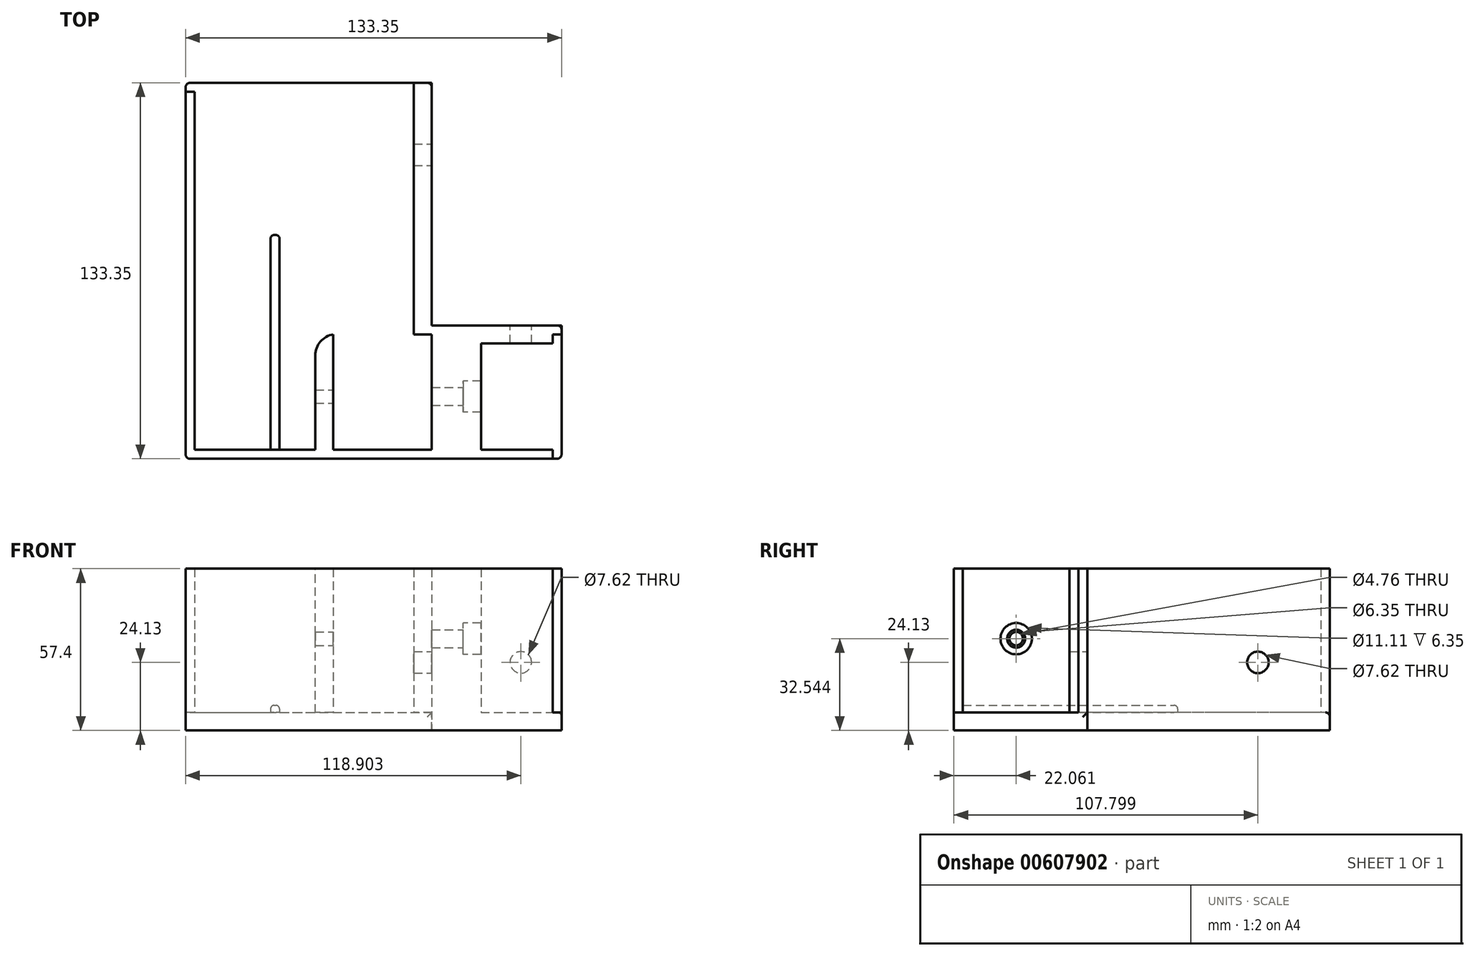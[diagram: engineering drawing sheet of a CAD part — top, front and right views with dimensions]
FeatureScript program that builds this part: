
annotation { "Feature Type Name" : "Feature", "Feature Type Description" : "" }
export const myFeature = defineFeature(function(context is Context, id is Id, definition is map)
    precondition{}
    {
        {
            var Q0;
            Q0=qCreatedBy(makeId("Top.planeOp"),FACE);
            var sketch = newSketch(context, id + "F0", { "sketchPlane" : qUnion([Q0])});
            skLineSegment(sketch, "E0.bottom", {"start": v(-63.28, 106.68) * mm, "end": v(70.07, 106.68) * mm});
            skLineSegment(sketch, "E0.top", {"start": v(-63.28, -26.67) * mm, "end": v(70.07, -26.67) * mm});
            skLineSegment(sketch, "E0.left", {"start": v(-63.28, 106.68) * mm, "end": v(-63.28, -26.67) * mm});
            skLineSegment(sketch, "E0.right", {"start": v(70.07, 106.68) * mm, "end": v(70.07, -26.67) * mm});
            skSolve(sketch);
        }
        {
            var Q0;
            Q0=makeQuery(id+"F0.imprint","IMPRINT",FACE,{"disambiguationData":[TD([[makeQuery(id+"F0.imprint","IMPRINT",EDGE,{"derivedFrom":sQuery(id+"F0.wireOp",EDGE,"E0.bottom")}),-1.0]])]});
            extrude(context, id + "F1", {"entities" : qUnion([Q0]), "depth" : 6.35 * mm, "offsetDistance" : 25.4 * mm});
        }
        {
            var Q0;
            Q0=makeQuery(id+"F1.opExtrude","CAP_FACE",FACE,{"disambiguationData":[OSD([sQuery(id+"F0.wireOp",EDGE,"E0.bottom"),sQuery(id+"F0.wireOp",EDGE,"E0.top"),sQuery(id+"F0.wireOp",EDGE,"E0.left"),sQuery(id+"F0.wireOp",EDGE,"E0.right")])],"isStart":false});
            var sketch = newSketch(context, id + "F2", { "sketchPlane" : qUnion([Q0])});
            skLineSegment(sketch, "E1.0", {"start": v(-60.1, 103.5) * mm, "end": v(66.9, 103.5) * mm});
            skLineSegment(sketch, "E1.1", {"start": v(-60.1, 103.5) * mm, "end": v(-60.1, -23.5) * mm});
            skLineSegment(sketch, "E1.2", {"start": v(-60.1, -23.5) * mm, "end": v(66.9, -23.5) * mm});
            skLineSegment(sketch, "E1.3", {"start": v(66.9, 103.5) * mm, "end": v(66.9, -23.5) * mm});
            skLineSegment(sketch, "E2.bottom", {"start": v(3.4, 103.5) * mm, "end": v(-10.9, 103.5) * mm});
            skLineSegment(sketch, "E2.top", {"start": v(3.4, -23.5) * mm, "end": v(-10.9, -23.5) * mm});
            skLineSegment(sketch, "E2.right", {"start": v(-10.9, 103.5) * mm, "end": v(-10.9, -23.5) * mm});
            skLineSegment(sketch, "E3.bottom", {"start": v(3.4, 103.5) * mm, "end": v(17.69, 103.5) * mm});
            skLineSegment(sketch, "E3.top", {"start": v(3.4, -23.5) * mm, "end": v(17.69, -23.5) * mm});
            skLineSegment(sketch, "E3.right", {"start": v(17.69, 103.5) * mm, "end": v(17.69, -23.5) * mm});
            skLineSegment(sketch, "E4.0", {"start": v(-17.25, 68.58) * mm, "end": v(-17.25, -23.5) * mm});
            skLineSegment(sketch, "E5.0", {"start": v(24.04, 68.58) * mm, "end": v(24.04, -23.5) * mm});
            skLineSegment(sketch, "E6", {"start": v(3.4, -23.5) * mm, "end": v(3.4, 103.5) * mm});
            skLineSegment(sketch, "E7", {"start": v(3.4, -23.5) * mm, "end": v(3.4, -3.18) * mm});
            skCircle(sketch, "E8", {"center": v(3.4, -3.18) * mm, "radius": 14.29 * mm});
            skLineSegment(sketch, "E9", {"start": v(3.4, 11.1) * mm, "end": v(3.4, 17.46) * mm});
            skLineSegment(sketch, "E10", {"start": v(17.69, 17.46) * mm, "end": v(-10.9, 17.46) * mm});
            skLineSegment(sketch, "E11", {"start": v(-10.9, 17.46) * mm, "end": v(-17.25, 17.46) * mm});
            skLineSegment(sketch, "E12", {"start": v(-60.1, 103.5) * mm, "end": v(-63.28, 103.5) * mm});
            skLineSegment(sketch, "E13", {"start": v(66.9, 103.5) * mm, "end": v(70.07, 103.5) * mm});
            skLineSegment(sketch, "E14", {"start": v(24.04, 68.58) * mm, "end": v(24.04, 103.5) * mm});
            skLineSegment(sketch, "E15", {"start": v(-17.25, 68.58) * mm, "end": v(-17.25, 103.5) * mm});
            skLineSegment(sketch, "E16", {"start": v(24.04, 103.5) * mm, "end": v(24.04, 106.68) * mm});
            skLineSegment(sketch, "E17", {"start": v(17.69, 103.5) * mm, "end": v(17.69, 106.68) * mm});
            skLineSegment(sketch, "E18", {"start": v(66.9, -23.5) * mm, "end": v(66.9, -26.67) * mm});
            skLineSegment(sketch, "E19", {"start": v(66.9, 17.46) * mm, "end": v(70.07, 17.46) * mm});
            skLineSegment(sketch, "E20.bottom", {"start": v(35.15, 17.46) * mm, "end": v(17.69, 17.46) * mm});
            skLineSegment(sketch, "E20.top", {"start": v(35.15, -23.5) * mm, "end": v(17.69, -23.5) * mm});
            skLineSegment(sketch, "E20.left", {"start": v(35.15, 17.46) * mm, "end": v(35.15, -23.5) * mm});
            skLineSegment(sketch, "E20.right", {"start": v(17.69, 17.46) * mm, "end": v(17.69, -23.5) * mm});
            skLineSegment(sketch, "E21", {"start": v(35.15, 17.46) * mm, "end": v(66.9, 17.46) * mm});
            skLineSegment(sketch, "E22", {"start": v(66.9, 17.46) * mm, "end": v(66.9, 20.63) * mm});
            skLineSegment(sketch, "E23", {"start": v(66.9, 20.63) * mm, "end": v(24.04, 20.63) * mm});
            skLineSegment(sketch, "E24", {"start": v(35.15, 17.46) * mm, "end": v(35.15, 14.28) * mm});
            skLineSegment(sketch, "E25", {"start": v(35.15, 14.28) * mm, "end": v(66.9, 14.28) * mm});
            skLineSegment(sketch, "E26.bottom", {"start": v(17.69, 103.5) * mm, "end": v(11.34, 103.5) * mm});
            skLineSegment(sketch, "E26.top", {"start": v(17.69, 97.15) * mm, "end": v(11.34, 97.15) * mm});
            skLineSegment(sketch, "E26.left", {"start": v(17.69, 103.5) * mm, "end": v(17.69, 97.15) * mm});
            skLineSegment(sketch, "E26.right", {"start": v(11.34, 103.5) * mm, "end": v(11.34, 97.15) * mm});
            skLineSegment(sketch, "E27.bottom", {"start": v(-60.1, 103.5) * mm, "end": v(-56.93, 103.5) * mm});
            skLineSegment(sketch, "E27.top", {"start": v(-60.1, 97.15) * mm, "end": v(-56.93, 97.15) * mm});
            skLineSegment(sketch, "E27.left", {"start": v(-60.1, 103.5) * mm, "end": v(-60.1, 97.15) * mm});
            skLineSegment(sketch, "E27.right", {"start": v(-56.93, 103.5) * mm, "end": v(-56.93, 97.15) * mm});
            skLineSegment(sketch, "E28", {"start": v(-60.1, 103.5) * mm, "end": v(-60.1, 106.68) * mm});
            skLineSegment(sketch, "E29", {"start": v(-17.25, -23.5) * mm, "end": v(-33.13, -23.5) * mm});
            skLineSegment(sketch, "E30", {"start": v(-33.13, -23.5) * mm, "end": v(-33.13, 52.7) * mm});
            skLineSegment(sketch, "E31", {"start": v(-33.13, 52.7) * mm, "end": v(-29.95, 52.7) * mm});
            skLineSegment(sketch, "E32", {"start": v(-29.95, 52.7) * mm, "end": v(-29.95, -23.5) * mm});
            skLineSegment(sketch, "E33", {"start": v(-33.13, -23.5) * mm, "end": v(-38.45, -23.5) * mm});
            skLineSegment(sketch, "E34", {"start": v(-33.13, -23.5) * mm, "end": v(-34.8, -23.5) * mm});
            skLineSegment(sketch, "E35", {"start": v(-34.8, -23.5) * mm, "end": v(-34.8, 52.7) * mm});
            skLineSegment(sketch, "E36", {"start": v(-34.8, 52.7) * mm, "end": v(-37.97, 52.7) * mm});
            skLineSegment(sketch, "E37", {"start": v(-37.97, 52.7) * mm, "end": v(-37.97, -23.5) * mm});
            skLineSegment(sketch, "E38", {"start": v(66.9, 20.63) * mm, "end": v(70.07, 20.63) * mm});
            skSolve(sketch);
        }
        {
            var Q0;
            {var subQ1=sQuery(id+"F2.wireOp",EDGE,"E1.2");var subQ3=sQuery(id+"F2.wireOp",EDGE,"E4.0");var subQ4=makeQuery(id+"F2.imprint","INTERSECT",VERTEX,{"derivedFrom":[subQ1,subQ3]});Q0=makeQuery(id+"F2.imprint","IMPRINT",FACE,{"disambiguationData":[TD([[makeQuery(id+"F2.imprint","IMPRINT",EDGE,{"disambiguationData":[TD([[subQ4,1.0]])],"derivedFrom":subQ3}),1.0]])]});}
            var Q1;
            {var subQ0=sQuery(id+"F2.wireOp",EDGE,"E11");Q1=makeQuery(id+"F2.imprint","IMPRINT",FACE,{"disambiguationData":[TD([[makeQuery(id+"F2.imprint","IMPRINT",EDGE,{"derivedFrom":subQ0}),1.0]])]});}
            var Q2;
            {var subQ5=sQuery(id+"F2.wireOp",EDGE,"E5.0");Q2=makeQuery(id+"F2.imprint","IMPRINT",FACE,{"disambiguationData":[TD([[makeQuery(id+"F2.imprint","IMPRINT",EDGE,{"derivedFrom":subQ5}),-1.0]])]});}
            var Q3;
            {var subQ5=sQuery(id+"F2.wireOp",EDGE,"E9");Q3=makeQuery(id+"F2.imprint","IMPRINT",FACE,{"disambiguationData":[TD([[makeQuery(id+"F2.imprint","IMPRINT",EDGE,{"derivedFrom":subQ5}),1.0]])]});}
            var Q4;
            {var subQ0=sQuery(id+"F2.wireOp",EDGE,"E2.top");Q4=makeQuery(id+"F2.imprint","IMPRINT",FACE,{"disambiguationData":[TD([[makeQuery(id+"F2.imprint","IMPRINT",EDGE,{"derivedFrom":subQ0}),-1.0]])]});}
            var Q5;
            {var subQ0=sQuery(id+"F2.wireOp",EDGE,"E3.top");Q5=makeQuery(id+"F2.imprint","IMPRINT",FACE,{"disambiguationData":[TD([[makeQuery(id+"F2.imprint","IMPRINT",EDGE,{"derivedFrom":subQ0}),1.0]])]});}
            var Q6;
            {var subQ5=sQuery(id+"F2.wireOp",EDGE,"E9");Q6=makeQuery(id+"F2.imprint","IMPRINT",FACE,{"disambiguationData":[TD([[makeQuery(id+"F2.imprint","IMPRINT",EDGE,{"derivedFrom":subQ5}),-1.0]])]});}
            var Q7;
            {var subQ6=sQuery(id+"F2.wireOp",EDGE,"E1.1");Q7=makeQuery(id+"F2.imprint","IMPRINT",FACE,{"disambiguationData":[TD([[makeQuery(id+"F2.imprint","IMPRINT",EDGE,{"derivedFrom":subQ6}),-1.0]])]});}
            var Q8;
            {var subQ2=sQuery(id+"F2.wireOp",EDGE,"E16");Q8=makeQuery(id+"F2.imprint","IMPRINT",FACE,{"disambiguationData":[TD([[makeQuery(id+"F2.imprint","IMPRINT",EDGE,{"derivedFrom":subQ2}),1.0]])]});}
            var Q9;
            {var subQ4=sQuery(id+"F2.wireOp",EDGE,"bkfMdUR7-iEIi-mk6J-M4my-fYpfkc70znqQ");Q9=makeQuery(id+"F2.imprint","IMPRINT",FACE,{"disambiguationData":[TD([[makeQuery(id+"F2.imprint","IMPRINT",EDGE,{"derivedFrom":subQ4}),-1.0]])]});}
            var Q10;
            {var subQ4=sQuery(id+"F2.wireOp",EDGE,"E20.top");var subQ6=sQuery(id+"F2.wireOp",EDGE,"E5.0");var subQ7=makeQuery(id+"F2.imprint","INTERSECT",VERTEX,{"derivedFrom":[subQ6,subQ4]});Q10=makeQuery(id+"F2.imprint","IMPRINT",FACE,{"disambiguationData":[TD([[makeQuery(id+"F2.imprint","IMPRINT",EDGE,{"disambiguationData":[TD([[subQ7,1.0]])],"derivedFrom":subQ6}),-1.0]])]});}
            var Q11;
            {var subQ3=sQuery(id+"F2.wireOp",EDGE,"E20.left");Q11=makeQuery(id+"F2.imprint","IMPRINT",FACE,{"disambiguationData":[TD([[makeQuery(id+"F2.imprint","IMPRINT",EDGE,{"derivedFrom":subQ3}),-1.0]])]});}
            var Q12;
            {var subQ0=sQuery(id+"F2.wireOp",EDGE,"E21");Q12=makeQuery(id+"F2.imprint","IMPRINT",FACE,{"disambiguationData":[TD([[makeQuery(id+"F2.imprint","IMPRINT",EDGE,{"derivedFrom":subQ0}),-1.0]])]});}
            var Q13;
            {var subQ0=sQuery(id+"F2.wireOp",EDGE,"E21");Q13=makeQuery(id+"F2.imprint","IMPRINT",FACE,{"disambiguationData":[TD([[makeQuery(id+"F2.imprint","IMPRINT",EDGE,{"derivedFrom":subQ0}),1.0]])]});}
            var Q14;
            Q14=makeQuery(id+"F2.imprint","IMPRINT",FACE,{"disambiguationData":[TD([[makeQuery(id+"F2.imprint","IMPRINT",EDGE,{"derivedFrom":sQuery(id+"F2.wireOp",EDGE,"E26.bottom")}),1.0]])]});
            var Q15;
            Q15=makeQuery(id+"F2.imprint","IMPRINT",FACE,{"disambiguationData":[TD([[makeQuery(id+"F2.imprint","IMPRINT",EDGE,{"derivedFrom":sQuery(id+"F2.wireOp",EDGE,"E27.bottom")}),-1.0]])]});
            var Q16;
            {var subQ0=sQuery(id+"F2.wireOp",EDGE,"E19");Q16=makeQuery(id+"F2.imprint","IMPRINT",FACE,{"disambiguationData":[TD([[makeQuery(id+"F2.imprint","IMPRINT",EDGE,{"derivedFrom":subQ0}),1.0]])]});}
            extrude(context, id + "F3", {"entities" : qUnion([Q0, Q1, Q2, Q3, Q4, Q5, Q6, Q7, Q8, Q9, Q10, Q11, Q12, Q13, Q14, Q15, Q16]), "operationType" : NewBodyOperationType.ADD, "depth" : 51.05 * mm, "offsetDistance" : 25.4 * mm});
        }
        {
            var Q0;
            Q0=makeQuery(id+"F3.opExtrude","SWEPT_EDGE",EDGE,{"disambiguationData":[OSD([sQuery(id+"F2.wireOp",EDGE,"E4.0"),sQuery(id+"F2.wireOp",EDGE,"E11")])]});
            fillet(context, id + "F4", {"entities" : qUnion([Q0]), "radius" : 7.62 * mm, "tangentPropagation" : true, "allowEdgeOverflow" : false});
        }
        {
            var Q0;
            Q0=makeQuery(id+"F3.opExtrude","SWEPT_FACE",FACE,{"disambiguationData":[OSD([sQuery(id+"F2.wireOp",EDGE,"E20.left")])]});
            var sketch = newSketch(context, id + "F5", { "sketchPlane" : qUnion([Q0])});
            skLineSegment(sketch, "E39", {"start": v(-4.6, 6.35) * mm, "end": v(-4.6, 30.16) * mm});
            skLineSegment(sketch, "E40", {"start": v(-4.6, 30.16) * mm, "end": v(-4.6, 32.54) * mm});
            skCircle(sketch, "E41", {"center": v(-4.6, 32.54) * mm, "radius": 2.38 * mm});
            skCircle(sketch, "E42", {"center": v(-4.6, 32.54) * mm, "radius": 3.18 * mm});
            skCircle(sketch, "E43", {"center": v(-4.6, 32.54) * mm, "radius": 7.14 * mm});
            skCircle(sketch, "E44", {"center": v(-4.6, 32.54) * mm, "radius": 5.56 * mm});
            skSolve(sketch);
        }
        {
            var Q0;
            Q0=makeQuery(id+"F5.imprint","IMPRINT",FACE,{"disambiguationData":[TD([[makeQuery(id+"F5.imprint","IMPRINT",EDGE,{"derivedFrom":sQuery(id+"F5.wireOp",EDGE,"E41")}),1.0]])]});
            var Q1;
            Q1=makeQuery(id+"F3.opExtrude","SWEPT_FACE",FACE,{"disambiguationData":[OSD([sQuery(id+"F2.wireOp",EDGE,"E4.0")])]});
            extrude(context, id + "F6", {"entities" : qUnion([Q0]), "operationType" : NewBodyOperationType.REMOVE, "endBound" : BoundingType.UP_TO_SURFACE, "oppositeDirection" : true, "depth" : 25.4 * mm, "endBoundEntityFace" : qUnion([Q1]), "offsetDistance" : 25.4 * mm});
        }
        {
            var Q0;
            Q0=makeQuery(id+"F5.imprint","IMPRINT",FACE,{"disambiguationData":[TD([[makeQuery(id+"F5.imprint","IMPRINT",EDGE,{"derivedFrom":sQuery(id+"F5.wireOp",EDGE,"E41")}),-1.0]])]});
            var Q1;
            Q1=makeQuery(id+"F3.opExtrude","SWEPT_FACE",FACE,{"disambiguationData":[OSD([sQuery(id+"F2.wireOp",EDGE,"E5.0"),sQuery(id+"F2.wireOp",EDGE,"E14")])]});
            extrude(context, id + "F7", {"entities" : qUnion([Q0]), "operationType" : NewBodyOperationType.REMOVE, "endBound" : BoundingType.UP_TO_SURFACE, "oppositeDirection" : true, "depth" : 25.4 * mm, "endBoundEntityFace" : qUnion([Q1]), "offsetDistance" : 25.4 * mm});
        }
        {
            var Q0;
            Q0=makeQuery(id+"F5.imprint","IMPRINT",FACE,{"disambiguationData":[TD([[makeQuery(id+"F5.imprint","IMPRINT",EDGE,{"derivedFrom":sQuery(id+"F5.wireOp",EDGE,"E43")}),1.0]])]});
            var Q1;
            Q1=makeQuery(id+"F5.imprint","IMPRINT",FACE,{"disambiguationData":[TD([[makeQuery(id+"F5.imprint","IMPRINT",EDGE,{"derivedFrom":sQuery(id+"F5.wireOp",EDGE,"E43")}),-1.0]])]});
            extrude(context, id + "F8", {"entities" : qUnion([Q0, Q1]), "operationType" : NewBodyOperationType.ADD, "depth" : 6.35 * mm, "offsetDistance" : 25.4 * mm});
        }
        {
            var Q0;
            {var subQ0=sQuery(id+"F2.wireOp",EDGE,"E33");Q0=makeQuery(id+"F2.imprint","IMPRINT",FACE,{"disambiguationData":[TD([[makeQuery(id+"F2.imprint","IMPRINT",EDGE,{"derivedFrom":subQ0}),-1.0]])]});}
            var Q1;
            {var subQ0=sQuery(id+"F2.wireOp",EDGE,"E30");Q1=makeQuery(id+"F2.imprint","IMPRINT",FACE,{"disambiguationData":[TD([[makeQuery(id+"F2.imprint","IMPRINT",EDGE,{"derivedFrom":subQ0}),-1.0]])]});}
            extrude(context, id + "F9", {"entities" : qUnion([Q0, Q1]), "operationType" : NewBodyOperationType.ADD, "depth" : 2.54 * mm, "offsetDistance" : 25.4 * mm});
        }
        {
            var Q0;
            Q0=makeQuery(id+"F9.opExtrude","CAP_EDGE",EDGE,{"disambiguationData":[OSD([sQuery(id+"F2.wireOp",EDGE,"E32")])],"isStart":false});
            var Q1;
            Q1=makeQuery(id+"F9.opExtrude","CAP_EDGE",EDGE,{"disambiguationData":[OSD([sQuery(id+"F2.wireOp",EDGE,"E30")])],"isStart":false});
            var Q2;
            Q2=makeQuery(id+"F9.opExtrude","CAP_EDGE",EDGE,{"disambiguationData":[OSD([sQuery(id+"F2.wireOp",EDGE,"E31")])],"isStart":false});
            var Q3;
            Q3=makeQuery(id+"F9.opExtrude","CAP_EDGE",EDGE,{"disambiguationData":[OSD([sQuery(id+"F2.wireOp",EDGE,"E36")])],"isStart":false});
            var Q4;
            Q4=makeQuery(id+"F9.opExtrude","CAP_EDGE",EDGE,{"disambiguationData":[OSD([sQuery(id+"F2.wireOp",EDGE,"E35")])],"isStart":false});
            var Q5;
            Q5=makeQuery(id+"F9.opExtrude","CAP_EDGE",EDGE,{"disambiguationData":[OSD([sQuery(id+"F2.wireOp",EDGE,"E37")])],"isStart":false});
            var Q6;
            Q6=makeQuery(id+"F9.opExtrude","SWEPT_EDGE",EDGE,{"disambiguationData":[OSD([sQuery(id+"F2.wireOp",EDGE,"E30"),sQuery(id+"F2.wireOp",EDGE,"E31")])]});
            var Q7;
            Q7=makeQuery(id+"F9.opExtrude","SWEPT_EDGE",EDGE,{"disambiguationData":[OSD([sQuery(id+"F2.wireOp",EDGE,"E35"),sQuery(id+"F2.wireOp",EDGE,"E36")])]});
            var Q8;
            Q8=makeQuery(id+"F9.opExtrude","SWEPT_EDGE",EDGE,{"disambiguationData":[OSD([sQuery(id+"F2.wireOp",EDGE,"E31"),sQuery(id+"F2.wireOp",EDGE,"E32")])]});
            var Q9;
            Q9=makeQuery(id+"F9.opExtrude","SWEPT_EDGE",EDGE,{"disambiguationData":[OSD([sQuery(id+"F2.wireOp",EDGE,"E36"),sQuery(id+"F2.wireOp",EDGE,"E37")])]});
            fillet(context, id + "F10", {"entities" : qUnion([Q0, Q1, Q2, Q3, Q4, Q5, Q6, Q7, Q8, Q9]), "radius" : 1.27 * mm, "tangentPropagation" : true, "allowEdgeOverflow" : false});
        }
        {
            var Q0;
            {var subQ0=sQuery(id+"F0.wireOp",EDGE,"E0.left");var subQ1=sQuery(id+"F0.wireOp",EDGE,"E0.bottom");Q0=makeQuery(id+"F3.boolean.opBoolean","MERGE",EDGE,{"derivedFrom":[makeQuery(id+"F1.opExtrude","SWEPT_EDGE",EDGE,{"disambiguationData":[OSD([subQ1,subQ0])]}),makeQuery(id+"F3.opExtrude","SWEPT_EDGE",EDGE,{"disambiguationData":[OSD([subQ1,subQ0])]})]});}
            var Q1;
            {var subQ0=sQuery(id+"F0.wireOp",EDGE,"E0.left");var subQ1=sQuery(id+"F0.wireOp",EDGE,"E0.top");Q1=makeQuery(id+"F3.boolean.opBoolean","MERGE",EDGE,{"derivedFrom":[makeQuery(id+"F1.opExtrude","SWEPT_EDGE",EDGE,{"disambiguationData":[OSD([subQ1,subQ0])]}),makeQuery(id+"F3.opExtrude","SWEPT_EDGE",EDGE,{"disambiguationData":[OSD([subQ1,subQ0])]})]});}
            var Q2;
            Q2=makeQuery(id+"F3.opExtrude","SWEPT_EDGE",EDGE,{"disambiguationData":[OSD([sQuery(id+"F0.wireOp",EDGE,"E0.bottom"),sQuery(id+"F2.wireOp",EDGE,"E16")])]});
            var Q3;
            Q3=makeQuery(id+"F3.opExtrude","SWEPT_EDGE",EDGE,{"disambiguationData":[OSD([sQuery(id+"F0.wireOp",EDGE,"E0.right"),sQuery(id+"F2.wireOp",EDGE,"E38")])]});
            var Q4;
            {var subQ0=sQuery(id+"F0.wireOp",EDGE,"E0.right");var subQ2=sQuery(id+"F0.wireOp",EDGE,"E0.bottom");Q4=makeQuery(id+"F3.boolean.opBoolean","SPLIT",EDGE,{"disambiguationData":[TD([makeQuery(id+"F1.opExtrude","SWEPT_FACE",FACE,{"disambiguationData":[OSD([subQ2])]})])],"derivedFrom":makeQuery(id+"F1.opExtrude","CAP_EDGE",EDGE,{"disambiguationData":[OSD([subQ0])],"isStart":false})});}
            var Q5;
            Q5=makeQuery(id+"F1.opExtrude","SWEPT_EDGE",EDGE,{"disambiguationData":[OSD([sQuery(id+"F0.wireOp",EDGE,"E0.bottom"),sQuery(id+"F0.wireOp",EDGE,"E0.right")])]});
            var Q6;
            {var subQ1=sQuery(id+"F0.wireOp",EDGE,"E0.right");var subQ3=sQuery(id+"F0.wireOp",EDGE,"E0.bottom");var subQ4=makeQuery(id+"F1.opExtrude","CAP_EDGE",EDGE,{"disambiguationData":[OSD([subQ3])],"isStart":false});Q6=makeQuery(id+"F3.boolean.opBoolean","SPLIT",EDGE,{"disambiguationData":[TD([makeQuery(id+"F1.opExtrude","SWEPT_FACE",FACE,{"disambiguationData":[OSD([subQ1])]})])],"derivedFrom":subQ4});}
            var Q7;
            Q7=makeQuery(id+"F1.opExtrude","SWEPT_EDGE",EDGE,{"disambiguationData":[OSD([sQuery(id+"F0.wireOp",EDGE,"E0.top"),sQuery(id+"F0.wireOp",EDGE,"E0.right")])]});
            fillet(context, id + "F11", {"entities" : qUnion([Q0, Q1, Q2, Q3, Q4, Q5, Q6, Q7]), "radius" : 1.59 * mm, "tangentPropagation" : true, "allowEdgeOverflow" : false});
        }
        {
            var Q0;
            Q0=makeQuery(id+"F3.opExtrude","SWEPT_FACE",FACE,{"disambiguationData":[OSD([sQuery(id+"F2.wireOp",EDGE,"E23"),sQuery(id+"F2.wireOp",EDGE,"E38")])]});
            var sketch = newSketch(context, id + "F12", { "sketchPlane" : qUnion([Q0])});
            skLineSegment(sketch, "E45", {"start": v(-55.62, 6.35) * mm, "end": v(-55.62, 24.13) * mm});
            skCircle(sketch, "E46", {"center": v(-55.62, 24.13) * mm, "radius": 3.81 * mm});
            skSolve(sketch);
        }
        {
            var Q0;
            Q0=makeQuery(id+"F12.imprint","IMPRINT",FACE,{"disambiguationData":[TD([[makeQuery(id+"F12.imprint","IMPRINT",EDGE,{"derivedFrom":sQuery(id+"F12.wireOp",EDGE,"E46")}),1.0]])]});
            var Q1;
            Q1=makeQuery(id+"F3.opExtrude","SWEPT_FACE",FACE,{"disambiguationData":[OSD([sQuery(id+"F2.wireOp",EDGE,"E25")])]});
            extrude(context, id + "F13", {"entities" : qUnion([Q0]), "operationType" : NewBodyOperationType.REMOVE, "endBound" : BoundingType.UP_TO_SURFACE, "oppositeDirection" : true, "depth" : 25.4 * mm, "endBoundEntityFace" : qUnion([Q1]), "offsetDistance" : 25.4 * mm});
        }
        {
            var Q0;
            Q0=makeQuery(id+"F3.opExtrude","SWEPT_FACE",FACE,{"disambiguationData":[OSD([sQuery(id+"F2.wireOp",EDGE,"E5.0"),sQuery(id+"F2.wireOp",EDGE,"E14"),sQuery(id+"F2.wireOp",EDGE,"E16")])]});
            var sketch = newSketch(context, id + "F14", { "sketchPlane" : qUnion([Q0])});
            skLineSegment(sketch, "E47", {"start": v(81.13, 6.35) * mm, "end": v(81.13, 24.13) * mm});
            skCircle(sketch, "E48", {"center": v(81.13, 24.13) * mm, "radius": 3.81 * mm});
            skSolve(sketch);
        }
        {
            var Q0;
            Q0=makeQuery(id+"F14.imprint","IMPRINT",FACE,{"disambiguationData":[TD([[makeQuery(id+"F14.imprint","IMPRINT",EDGE,{"derivedFrom":sQuery(id+"F14.wireOp",EDGE,"E48")}),1.0]])]});
            var Q1;
            Q1=makeQuery(id+"F3.opExtrude","SWEPT_FACE",FACE,{"disambiguationData":[OSD([sQuery(id+"F2.wireOp",EDGE,"E3.right")])]});
            extrude(context, id + "F15", {"entities" : qUnion([Q0]), "operationType" : NewBodyOperationType.REMOVE, "endBound" : BoundingType.UP_TO_SURFACE, "oppositeDirection" : true, "depth" : 25.4 * mm, "endBoundEntityFace" : qUnion([Q1]), "offsetDistance" : 25.4 * mm});
        }
        {
            var Q0;
            {var subQ0=sQuery(id+"F2.wireOp",EDGE,"E14");Q0=makeQuery(id+"F2.imprint","IMPRINT",FACE,{"disambiguationData":[TD([[makeQuery(id+"F2.imprint","IMPRINT",EDGE,{"derivedFrom":subQ0}),-1.0]])]});}
            var Q1;
            {var subQ0=sQuery(id+"F2.wireOp",EDGE,"E13");Q1=makeQuery(id+"F2.imprint","IMPRINT",FACE,{"disambiguationData":[TD([[makeQuery(id+"F2.imprint","IMPRINT",EDGE,{"derivedFrom":subQ0}),-1.0]])]});}
            var Q2;
            {var subQ4=sQuery(id+"F2.wireOp",EDGE,"E13");Q2=makeQuery(id+"F2.imprint","IMPRINT",FACE,{"disambiguationData":[TD([[makeQuery(id+"F2.imprint","IMPRINT",EDGE,{"derivedFrom":subQ4}),1.0]])]});}
            extrude(context, id + "F16", {"entities" : qUnion([Q0, Q1, Q2]), "operationType" : NewBodyOperationType.REMOVE, "oppositeDirection" : true, "depth" : 25.4 * mm, "offsetDistance" : 25.4 * mm});
        }
        {
            var Q0;
            Q0=makeQuery(id+"F16.boolean.opBoolean","COPY",EDGE,{"derivedFrom":makeQuery(id+"F16.opExtrude","SWEPT_EDGE",EDGE,{"disambiguationData":[OSD([sQuery(id+"F0.wireOp",EDGE,"E0.right"),sQuery(id+"F2.wireOp",EDGE,"E38")])]})});
            var Q1;
            Q1=makeQuery(id+"F16.boolean.opBoolean","COPY",EDGE,{"derivedFrom":makeQuery(id+"F16.opExtrude","SWEPT_EDGE",EDGE,{"disambiguationData":[OSD([sQuery(id+"F0.wireOp",EDGE,"E0.bottom"),sQuery(id+"F2.wireOp",EDGE,"E16")])]})});
            var Q2;
            Q2=makeQuery(id+"F1.opExtrude","SWEPT_EDGE",EDGE,{"disambiguationData":[OSD([sQuery(id+"F0.wireOp",EDGE,"E0.bottom"),sQuery(id+"F0.wireOp",EDGE,"E0.left")])]});
            fillet(context, id + "F17", {"entities" : qUnion([Q0, Q1, Q2]), "radius" : 1.59 * mm, "tangentPropagation" : true, "allowEdgeOverflow" : false});
        }
    });
